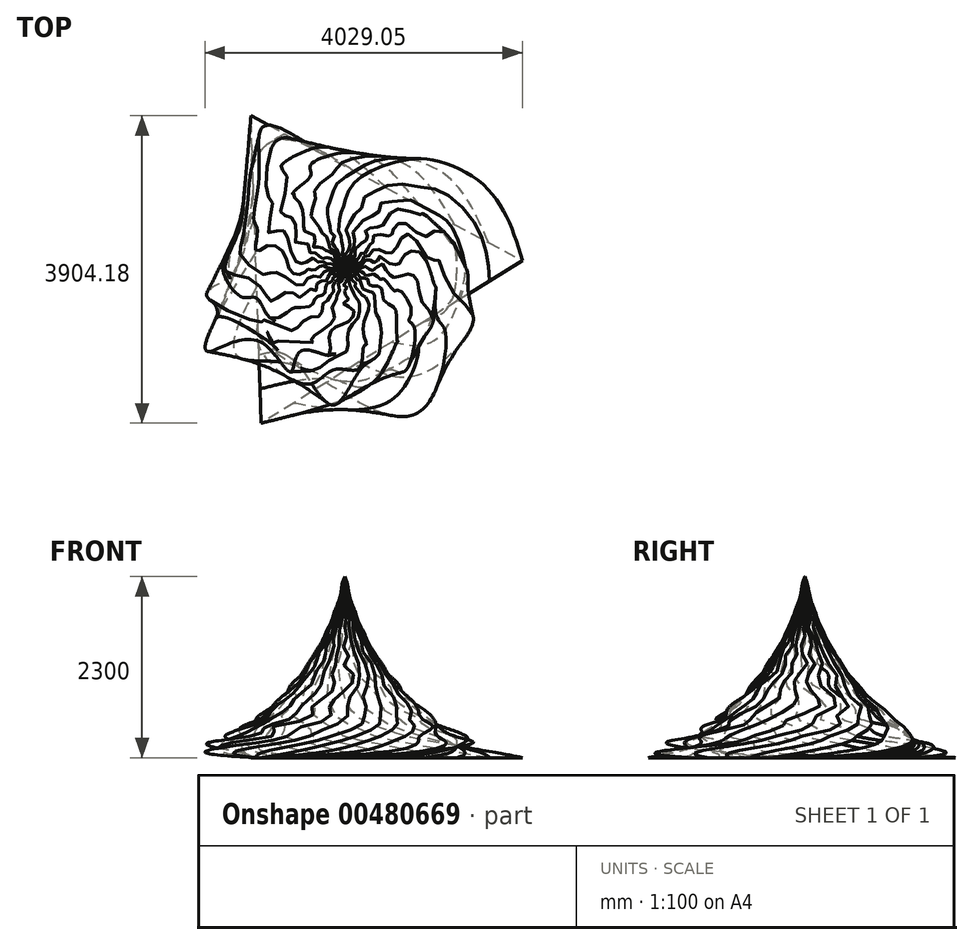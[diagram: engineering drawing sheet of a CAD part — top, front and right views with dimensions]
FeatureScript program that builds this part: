
annotation { "Feature Type Name" : "Feature", "Feature Type Description" : "" }
export const myFeature = defineFeature(function(context is Context, id is Id, definition is map)
    precondition{}
    {
        {
            var Q0;
            Q0=qCreatedBy(makeId("Top.planeOp"),FACE);
            var sketch = newSketch(context, id + "F0", { "sketchPlane" : qUnion([Q0])});
            skCircle(sketch, "E0.cCircle", {"center": v(0, 0) * mm, "radius": 2255.36 * mm, "construction": true});
            skLineSegment(sketch, "E0.0", {"start": v(2254.08, 76) * mm, "end": v(-1061.23, -1990.09) * mm});
            skLineSegment(sketch, "E0.1", {"start": v(-1061.23, -1990.09) * mm, "end": v(-1192.85, 1914.1) * mm});
            skLineSegment(sketch, "E0.2", {"start": v(-1192.85, 1914.1) * mm, "end": v(2254.08, 76) * mm});
            skSolve(sketch);
        }
        {
            var Q0;
            Q0=makeQuery(id+"F0.imprint","IMPRINT",FACE,{"disambiguationData":[TD([[makeQuery(id+"F0.imprint","IMPRINT",EDGE,{"derivedFrom":sQuery(id+"F0.wireOp",EDGE,"E0.0")}),-1.0]])]});
            cPlane(context, id + "F1", {"entities" : qUnion([Q0]), "cplaneType" : CPlaneType.OFFSET, "offset" : 100 * mm, "width" : 152.4 * mm, "height" : 152.4 * mm});
        }
        {
            var Q0;
            Q0=qCreatedBy(id+"F1.planeOp",FACE);
            var sketch = newSketch(context, id + "F2", { "sketchPlane" : qUnion([Q0])});
            skCircle(sketch, "E1.cCircle", {"center": v(0, 0) * mm, "radius": 2022.94 * mm, "construction": true});
            skLineSegment(sketch, "E1.0", {"start": v(-1078.65, 1711.37) * mm, "end": v(1711.37, 1078.65) * mm});
            skLineSegment(sketch, "E1.1", {"start": v(1711.37, 1078.65) * mm, "end": v(1078.65, -1711.37) * mm});
            skLineSegment(sketch, "E1.2", {"start": v(1078.65, -1711.37) * mm, "end": v(-1711.37, -1078.65) * mm});
            skLineSegment(sketch, "E1.3", {"start": v(-1711.37, -1078.65) * mm, "end": v(-1078.65, 1711.37) * mm});
            skSolve(sketch);
        }
        {
            var Q0;
            Q0=qCreatedBy(id+"F1.planeOp",FACE);
            cPlane(context, id + "F3", {"entities" : qUnion([Q0]), "cplaneType" : CPlaneType.OFFSET, "offset" : 100 * mm, "width" : 150 * mm, "height" : 150 * mm});
        }
        {
            var Q0;
            Q0=qCreatedBy(id+"F3.planeOp",FACE);
            var sketch = newSketch(context, id + "F4", { "sketchPlane" : qUnion([Q0])});
            skCircle(sketch, "E2.cCircle", {"center": v(0, 0) * mm, "radius": 1754.18 * mm, "construction": true});
            skLineSegment(sketch, "E2.0", {"start": v(-941.86, 1479.87) * mm, "end": v(1116.4, 1353.07) * mm});
            skLineSegment(sketch, "E2.1", {"start": v(1116.4, 1353.07) * mm, "end": v(1631.83, -643.63) * mm});
            skLineSegment(sketch, "E2.2", {"start": v(1631.83, -643.63) * mm, "end": v(-107.87, -1750.86) * mm});
            skLineSegment(sketch, "E2.3", {"start": v(-107.87, -1750.86) * mm, "end": v(-1698.5, -438.46) * mm});
            skLineSegment(sketch, "E2.4", {"start": v(-1698.5, -438.46) * mm, "end": v(-941.86, 1479.87) * mm});
            skSolve(sketch);
        }
        {
            var Q0;
            Q0=qCreatedBy(id+"F3.planeOp",FACE);
            cPlane(context, id + "F5", {"entities" : qUnion([Q0]), "cplaneType" : CPlaneType.OFFSET, "offset" : 100 * mm, "width" : 150 * mm, "height" : 150 * mm});
        }
        {
            var Q0;
            Q0=qCreatedBy(id+"F5.planeOp",FACE);
            var sketch = newSketch(context, id + "F6", { "sketchPlane" : qUnion([Q0])});
            skCircle(sketch, "E3.cCircle", {"center": v(0, 0) * mm, "radius": 1495.6 * mm, "construction": true});
            skLineSegment(sketch, "E3.0", {"start": v(-815.6, 1253.64) * mm, "end": v(677.89, 1333.14) * mm});
            skLineSegment(sketch, "E3.1", {"start": v(677.89, 1333.14) * mm, "end": v(1493.48, 79.5) * mm});
            skLineSegment(sketch, "E3.2", {"start": v(1493.48, 79.5) * mm, "end": v(815.6, -1253.64) * mm});
            skLineSegment(sketch, "E3.3", {"start": v(815.6, -1253.64) * mm, "end": v(-677.89, -1333.14) * mm});
            skLineSegment(sketch, "E3.4", {"start": v(-677.89, -1333.14) * mm, "end": v(-1493.48, -79.5) * mm});
            skLineSegment(sketch, "E3.5", {"start": v(-1493.48, -79.5) * mm, "end": v(-815.6, 1253.64) * mm});
            skSolve(sketch);
        }
        {
            var Q0;
            Q0=qCreatedBy(id+"F5.planeOp",FACE);
            cPlane(context, id + "F7", {"entities" : qUnion([Q0]), "cplaneType" : CPlaneType.OFFSET, "offset" : 100 * mm, "width" : 150 * mm, "height" : 150 * mm});
        }
        {
            var Q0;
            Q0=qCreatedBy(id+"F7.planeOp",FACE);
            var sketch = newSketch(context, id + "F8", { "sketchPlane" : qUnion([Q0])});
            skCircle(sketch, "E4.cCircle", {"center": v(0, 0) * mm, "radius": 1305.8 * mm, "construction": true});
            skLineSegment(sketch, "E4.0", {"start": v(-726.15, 1085.28) * mm, "end": v(395.76, 1244.39) * mm});
            skLineSegment(sketch, "E4.1", {"start": v(395.76, 1244.39) * mm, "end": v(1219.65, 466.45) * mm});
            skLineSegment(sketch, "E4.2", {"start": v(1219.65, 466.45) * mm, "end": v(1125.12, -662.74) * mm});
            skLineSegment(sketch, "E4.3", {"start": v(1125.12, -662.74) * mm, "end": v(183.35, -1292.87) * mm});
            skLineSegment(sketch, "E4.4", {"start": v(183.35, -1292.87) * mm, "end": v(-896.49, -949.44) * mm});
            skLineSegment(sketch, "E4.5", {"start": v(-896.49, -949.44) * mm, "end": v(-1301.25, 108.93) * mm});
            skLineSegment(sketch, "E4.6", {"start": v(-1301.25, 108.93) * mm, "end": v(-726.15, 1085.28) * mm});
            skSolve(sketch);
        }
        {
            var Q0;
            Q0=qCreatedBy(id+"F7.planeOp",FACE);
            cPlane(context, id + "F9", {"entities" : qUnion([Q0]), "cplaneType" : CPlaneType.OFFSET, "offset" : 100 * mm, "width" : 150 * mm, "height" : 150 * mm});
        }
        {
            var Q0;
            Q0=qCreatedBy(id+"F9.planeOp",FACE);
            var sketch = newSketch(context, id + "F10", { "sketchPlane" : qUnion([Q0])});
            skCircle(sketch, "E5.cCircle", {"center": v(0, 0) * mm, "radius": 1139.43 * mm, "construction": true});
            skLineSegment(sketch, "E5.0", {"start": v(-661.29, 927.9) * mm, "end": v(188.52, 1123.72) * mm});
            skLineSegment(sketch, "E5.1", {"start": v(188.52, 1123.72) * mm, "end": v(927.9, 661.29) * mm});
            skLineSegment(sketch, "E5.2", {"start": v(927.9, 661.29) * mm, "end": v(1123.72, -188.52) * mm});
            skLineSegment(sketch, "E5.3", {"start": v(1123.72, -188.52) * mm, "end": v(661.29, -927.9) * mm});
            skLineSegment(sketch, "E5.4", {"start": v(661.29, -927.9) * mm, "end": v(-188.52, -1123.72) * mm});
            skLineSegment(sketch, "E5.5", {"start": v(-188.52, -1123.72) * mm, "end": v(-927.9, -661.29) * mm});
            skLineSegment(sketch, "E5.6", {"start": v(-927.9, -661.29) * mm, "end": v(-1123.72, 188.52) * mm});
            skLineSegment(sketch, "E5.7", {"start": v(-1123.72, 188.52) * mm, "end": v(-661.29, 927.9) * mm});
            skSolve(sketch);
        }
        {
            var Q0;
            Q0=qCreatedBy(id+"F9.planeOp",FACE);
            cPlane(context, id + "F11", {"entities" : qUnion([Q0]), "cplaneType" : CPlaneType.OFFSET, "offset" : 100 * mm, "width" : 150 * mm, "height" : 150 * mm});
        }
        {
            var Q0;
            Q0=qCreatedBy(id+"F11.planeOp",FACE);
            var sketch = newSketch(context, id + "F12", { "sketchPlane" : qUnion([Q0])});
            skCircle(sketch, "E6.cCircle", {"center": v(0, 0) * mm, "radius": 1027.53 * mm, "construction": true});
            skLineSegment(sketch, "E6.0", {"start": v(-594.62, 838) * mm, "end": v(83.15, 1024.16) * mm});
            skLineSegment(sketch, "E6.1", {"start": v(83.15, 1024.16) * mm, "end": v(722.02, 731.1) * mm});
            skLineSegment(sketch, "E6.2", {"start": v(722.02, 731.1) * mm, "end": v(1023.04, 95.95) * mm});
            skLineSegment(sketch, "E6.3", {"start": v(1023.04, 95.95) * mm, "end": v(845.37, -584.1) * mm});
            skLineSegment(sketch, "E6.4", {"start": v(845.37, -584.1) * mm, "end": v(272.15, -990.84) * mm});
            skLineSegment(sketch, "E6.5", {"start": v(272.15, -990.84) * mm, "end": v(-428.42, -933.96) * mm});
            skLineSegment(sketch, "E6.6", {"start": v(-428.42, -933.96) * mm, "end": v(-928.53, -440.07) * mm});
            skLineSegment(sketch, "E6.7", {"start": v(-928.53, -440.07) * mm, "end": v(-994.16, 259.73) * mm});
            skLineSegment(sketch, "E6.8", {"start": v(-994.16, 259.73) * mm, "end": v(-594.62, 838) * mm});
            skSolve(sketch);
        }
        {
            var Q0;
            Q0=qCreatedBy(id+"F11.planeOp",FACE);
            cPlane(context, id + "F13", {"entities" : qUnion([Q0]), "cplaneType" : CPlaneType.OFFSET, "offset" : 100 * mm, "width" : 150 * mm, "height" : 150 * mm});
        }
        {
            var Q0;
            Q0=qCreatedBy(id+"F13.planeOp",FACE);
            cPlane(context, id + "F14", {"entities" : qUnion([Q0]), "cplaneType" : CPlaneType.OFFSET, "offset" : 100 * mm, "width" : 150 * mm, "height" : 150 * mm});
        }
        {
            var Q0;
            Q0=qCreatedBy(id+"F14.planeOp",FACE);
            var sketch = newSketch(context, id + "F15", { "sketchPlane" : qUnion([Q0])});
            skCircle(sketch, "E7.cCircle", {"center": v(0, 0) * mm, "radius": 779.03 * mm, "construction": true});
            skLineSegment(sketch, "E7.0", {"start": v(-431.52, 648.6) * mm, "end": v(-12.36, 778.93) * mm});
            skLineSegment(sketch, "E7.1", {"start": v(-12.36, 778.93) * mm, "end": v(410.72, 661.96) * mm});
            skLineSegment(sketch, "E7.2", {"start": v(410.72, 661.96) * mm, "end": v(703.4, 334.82) * mm});
            skLineSegment(sketch, "E7.3", {"start": v(703.4, 334.82) * mm, "end": v(772.76, -98.62) * mm});
            skLineSegment(sketch, "E7.4", {"start": v(772.76, -98.62) * mm, "end": v(596.77, -500.75) * mm});
            skLineSegment(sketch, "E7.5", {"start": v(596.77, -500.75) * mm, "end": v(231.3, -743.9) * mm});
            skLineSegment(sketch, "E7.6", {"start": v(231.3, -743.9) * mm, "end": v(-207.6, -750.86) * mm});
            skLineSegment(sketch, "E7.7", {"start": v(-207.6, -750.86) * mm, "end": v(-580.58, -519.43) * mm});
            skLineSegment(sketch, "E7.8", {"start": v(-580.58, -519.43) * mm, "end": v(-769.24, -123.09) * mm});
            skLineSegment(sketch, "E7.9", {"start": v(-769.24, -123.09) * mm, "end": v(-713.68, 312.34) * mm});
            skLineSegment(sketch, "E7.10", {"start": v(-713.68, 312.34) * mm, "end": v(-431.52, 648.6) * mm});
            skSolve(sketch);
        }
        {
            var Q0;
            Q0=qCreatedBy(id+"F14.planeOp",FACE);
            cPlane(context, id + "F16", {"entities" : qUnion([Q0]), "cplaneType" : CPlaneType.OFFSET, "offset" : 100 * mm, "width" : 150 * mm, "height" : 150 * mm});
        }
        {
            var Q0;
            Q0=qCreatedBy(id+"F16.planeOp",FACE);
            var sketch = newSketch(context, id + "F17", { "sketchPlane" : qUnion([Q0])});
            skCircle(sketch, "E8.cCircle", {"center": v(0, 0) * mm, "radius": 703.15 * mm, "construction": true});
            skLineSegment(sketch, "E8.0", {"start": v(-389.43, 585.46) * mm, "end": v(-44.53, 701.74) * mm});
            skLineSegment(sketch, "E8.1", {"start": v(-44.53, 701.74) * mm, "end": v(312.3, 629.99) * mm});
            skLineSegment(sketch, "E8.2", {"start": v(312.3, 629.99) * mm, "end": v(585.46, 389.43) * mm});
            skLineSegment(sketch, "E8.3", {"start": v(585.46, 389.43) * mm, "end": v(701.74, 44.53) * mm});
            skLineSegment(sketch, "E8.4", {"start": v(701.74, 44.53) * mm, "end": v(629.99, -312.3) * mm});
            skLineSegment(sketch, "E8.5", {"start": v(629.99, -312.3) * mm, "end": v(389.43, -585.46) * mm});
            skLineSegment(sketch, "E8.6", {"start": v(389.43, -585.46) * mm, "end": v(44.53, -701.74) * mm});
            skLineSegment(sketch, "E8.7", {"start": v(44.53, -701.74) * mm, "end": v(-312.3, -629.99) * mm});
            skLineSegment(sketch, "E8.8", {"start": v(-312.3, -629.99) * mm, "end": v(-585.46, -389.43) * mm});
            skLineSegment(sketch, "E8.9", {"start": v(-585.46, -389.43) * mm, "end": v(-701.74, -44.53) * mm});
            skLineSegment(sketch, "E8.10", {"start": v(-701.74, -44.53) * mm, "end": v(-629.99, 312.3) * mm});
            skLineSegment(sketch, "E8.11", {"start": v(-629.99, 312.3) * mm, "end": v(-389.43, 585.46) * mm});
            skSolve(sketch);
        }
        {
            var Q0;
            Q0=qCreatedBy(id+"F16.planeOp",FACE);
            cPlane(context, id + "F18", {"entities" : qUnion([Q0]), "cplaneType" : CPlaneType.OFFSET, "offset" : 100 * mm, "width" : 150 * mm, "height" : 150 * mm});
        }
        {
            var Q0;
            Q0=qCreatedBy(id+"F18.planeOp",FACE);
            cPlane(context, id + "F19", {"entities" : qUnion([Q0]), "cplaneType" : CPlaneType.OFFSET, "offset" : 100 * mm, "width" : 150 * mm, "height" : 150 * mm});
        }
        {
            var Q0;
            Q0=qCreatedBy(id+"F19.planeOp",FACE);
            var sketch = newSketch(context, id + "F20", { "sketchPlane" : qUnion([Q0])});
            skCircle(sketch, "E9.cCircle", {"center": v(0, 0) * mm, "radius": 528.05 * mm, "construction": true});
            skLineSegment(sketch, "E9.0", {"start": v(-294.73, 438.15) * mm, "end": v(-75.44, 522.63) * mm});
            skLineSegment(sketch, "E9.1", {"start": v(-75.44, 522.63) * mm, "end": v(158.8, 503.6) * mm});
            skLineSegment(sketch, "E9.2", {"start": v(158.8, 503.6) * mm, "end": v(361.58, 384.83) * mm});
            skLineSegment(sketch, "E9.3", {"start": v(361.58, 384.83) * mm, "end": v(492.74, 189.84) * mm});
            skLineSegment(sketch, "E9.4", {"start": v(492.74, 189.84) * mm, "end": v(526.32, -42.75) * mm});
            skLineSegment(sketch, "E9.5", {"start": v(526.32, -42.75) * mm, "end": v(455.65, -266.88) * mm});
            skLineSegment(sketch, "E9.6", {"start": v(455.65, -266.88) * mm, "end": v(294.73, -438.15) * mm});
            skLineSegment(sketch, "E9.7", {"start": v(294.73, -438.15) * mm, "end": v(75.44, -522.63) * mm});
            skLineSegment(sketch, "E9.8", {"start": v(75.44, -522.63) * mm, "end": v(-158.8, -503.6) * mm});
            skLineSegment(sketch, "E9.9", {"start": v(-158.8, -503.6) * mm, "end": v(-361.58, -384.83) * mm});
            skLineSegment(sketch, "E9.10", {"start": v(-361.58, -384.83) * mm, "end": v(-492.74, -189.84) * mm});
            skLineSegment(sketch, "E9.11", {"start": v(-492.74, -189.84) * mm, "end": v(-526.32, 42.75) * mm});
            skLineSegment(sketch, "E9.12", {"start": v(-526.32, 42.75) * mm, "end": v(-455.65, 266.88) * mm});
            skLineSegment(sketch, "E9.13", {"start": v(-455.65, 266.88) * mm, "end": v(-294.73, 438.15) * mm});
            skSolve(sketch);
        }
        {
            var Q0;
            Q0=qCreatedBy(id+"F19.planeOp",FACE);
            cPlane(context, id + "F21", {"entities" : qUnion([Q0]), "cplaneType" : CPlaneType.OFFSET, "offset" : 100 * mm, "width" : 150 * mm, "height" : 150 * mm});
        }
        {
            var Q0;
            Q0=qCreatedBy(id+"F21.planeOp",FACE);
            var sketch = newSketch(context, id + "F22", { "sketchPlane" : qUnion([Q0])});
            skCircle(sketch, "E10.cCircle", {"center": v(0, 0) * mm, "radius": 471.14 * mm, "construction": true});
            skLineSegment(sketch, "E10.0", {"start": v(-263.16, 390.8) * mm, "end": v(-81.46, 464.05) * mm});
            skLineSegment(sketch, "E10.1", {"start": v(-81.46, 464.05) * mm, "end": v(114.33, 457.06) * mm});
            skLineSegment(sketch, "E10.2", {"start": v(114.33, 457.06) * mm, "end": v(290.35, 371.04) * mm});
            skLineSegment(sketch, "E10.3", {"start": v(290.35, 371.04) * mm, "end": v(416.16, 220.87) * mm});
            skLineSegment(sketch, "E10.4", {"start": v(416.16, 220.87) * mm, "end": v(470.02, 32.5) * mm});
            skLineSegment(sketch, "E10.5", {"start": v(470.02, 32.5) * mm, "end": v(442.6, -161.48) * mm});
            skLineSegment(sketch, "E10.6", {"start": v(442.6, -161.48) * mm, "end": v(338.66, -327.54) * mm});
            skLineSegment(sketch, "E10.7", {"start": v(338.66, -327.54) * mm, "end": v(176.16, -436.97) * mm});
            skLineSegment(sketch, "E10.8", {"start": v(176.16, -436.97) * mm, "end": v(-16.8, -470.84) * mm});
            skLineSegment(sketch, "E10.9", {"start": v(-16.8, -470.84) * mm, "end": v(-206.86, -423.3) * mm});
            skLineSegment(sketch, "E10.10", {"start": v(-206.86, -423.3) * mm, "end": v(-361.15, -302.57) * mm});
            skLineSegment(sketch, "E10.11", {"start": v(-361.15, -302.57) * mm, "end": v(-452.99, -129.52) * mm});
            skLineSegment(sketch, "E10.12", {"start": v(-452.99, -129.52) * mm, "end": v(-466.5, 65.93) * mm});
            skLineSegment(sketch, "E10.13", {"start": v(-466.5, 65.93) * mm, "end": v(-399.36, 249.97) * mm});
            skLineSegment(sketch, "E10.14", {"start": v(-399.36, 249.97) * mm, "end": v(-263.16, 390.8) * mm});
            skSolve(sketch);
        }
        {
            var Q0;
            Q0=qCreatedBy(id+"F21.planeOp",FACE);
            cPlane(context, id + "F23", {"entities" : qUnion([Q0]), "cplaneType" : CPlaneType.OFFSET, "offset" : 100 * mm, "width" : 150 * mm, "height" : 150 * mm});
        }
        {
            var Q0;
            Q0=qCreatedBy(id+"F23.planeOp",FACE);
            var sketch = newSketch(context, id + "F24", { "sketchPlane" : qUnion([Q0])});
            skCircle(sketch, "E11.cCircle", {"center": v(0, 0) * mm, "radius": 402 * mm, "construction": true});
            skLineSegment(sketch, "E11.0", {"start": v(-200.02, 348.7) * mm, "end": v(-51.36, 398.7) * mm});
            skLineSegment(sketch, "E11.1", {"start": v(-51.36, 398.7) * mm, "end": v(105.13, 388.01) * mm});
            skLineSegment(sketch, "E11.2", {"start": v(105.13, 388.01) * mm, "end": v(245.62, 318.24) * mm});
            skLineSegment(sketch, "E11.3", {"start": v(245.62, 318.24) * mm, "end": v(348.7, 200.02) * mm});
            skLineSegment(sketch, "E11.4", {"start": v(348.7, 200.02) * mm, "end": v(398.7, 51.36) * mm});
            skLineSegment(sketch, "E11.5", {"start": v(398.7, 51.36) * mm, "end": v(388.01, -105.13) * mm});
            skLineSegment(sketch, "E11.6", {"start": v(388.01, -105.13) * mm, "end": v(318.24, -245.62) * mm});
            skLineSegment(sketch, "E11.7", {"start": v(318.24, -245.62) * mm, "end": v(200.02, -348.7) * mm});
            skLineSegment(sketch, "E11.8", {"start": v(200.02, -348.7) * mm, "end": v(51.36, -398.7) * mm});
            skLineSegment(sketch, "E11.9", {"start": v(51.36, -398.7) * mm, "end": v(-105.13, -388.01) * mm});
            skLineSegment(sketch, "E11.10", {"start": v(-105.13, -388.01) * mm, "end": v(-245.62, -318.24) * mm});
            skLineSegment(sketch, "E11.11", {"start": v(-245.62, -318.24) * mm, "end": v(-348.7, -200.02) * mm});
            skLineSegment(sketch, "E11.12", {"start": v(-348.7, -200.02) * mm, "end": v(-398.7, -51.36) * mm});
            skLineSegment(sketch, "E11.13", {"start": v(-398.7, -51.36) * mm, "end": v(-388.01, 105.13) * mm});
            skLineSegment(sketch, "E11.14", {"start": v(-388.01, 105.13) * mm, "end": v(-318.24, 245.62) * mm});
            skLineSegment(sketch, "E11.15", {"start": v(-318.24, 245.62) * mm, "end": v(-200.02, 348.7) * mm});
            skSolve(sketch);
        }
        {
            var Q0;
            Q0=qCreatedBy(id+"F23.planeOp",FACE);
            cPlane(context, id + "F25", {"entities" : qUnion([Q0]), "cplaneType" : CPlaneType.OFFSET, "offset" : 100 * mm, "width" : 150 * mm, "height" : 150 * mm});
        }
        {
            var Q0;
            Q0=qCreatedBy(id+"F25.planeOp",FACE);
            var sketch = newSketch(context, id + "F26", { "sketchPlane" : qUnion([Q0])});
            skCircle(sketch, "E12.cCircle", {"center": v(0, 0) * mm, "radius": 338.09 * mm, "construction": true});
            skLineSegment(sketch, "E12.0", {"start": v(-163.2, 296.1) * mm, "end": v(-45.21, 335.05) * mm});
            skLineSegment(sketch, "E12.1", {"start": v(-45.21, 335.05) * mm, "end": v(78.87, 328.76) * mm});
            skLineSegment(sketch, "E12.2", {"start": v(78.87, 328.76) * mm, "end": v(192.3, 278.07) * mm});
            skLineSegment(sketch, "E12.3", {"start": v(192.3, 278.07) * mm, "end": v(279.77, 189.82) * mm});
            skLineSegment(sketch, "E12.4", {"start": v(279.77, 189.82) * mm, "end": v(329.45, 75.94) * mm});
            skLineSegment(sketch, "E12.5", {"start": v(329.45, 75.94) * mm, "end": v(334.64, -48.2) * mm});
            skLineSegment(sketch, "E12.6", {"start": v(334.64, -48.2) * mm, "end": v(294.63, -165.83) * mm});
            skLineSegment(sketch, "E12.7", {"start": v(294.63, -165.83) * mm, "end": v(214.82, -261.06) * mm});
            skLineSegment(sketch, "E12.8", {"start": v(214.82, -261.06) * mm, "end": v(106.01, -321.04) * mm});
            skLineSegment(sketch, "E12.9", {"start": v(106.01, -321.04) * mm, "end": v(-17.12, -337.66) * mm});
            skLineSegment(sketch, "E12.10", {"start": v(-17.12, -337.66) * mm, "end": v(-137.94, -308.67) * mm});
            skLineSegment(sketch, "E12.11", {"start": v(-137.94, -308.67) * mm, "end": v(-240.13, -238) * mm});
            skLineSegment(sketch, "E12.12", {"start": v(-240.13, -238) * mm, "end": v(-309.89, -135.18) * mm});
            skLineSegment(sketch, "E12.13", {"start": v(-309.89, -135.18) * mm, "end": v(-337.8, -14.1) * mm});
            skLineSegment(sketch, "E12.14", {"start": v(-337.8, -14.1) * mm, "end": v(-320.08, 108.87) * mm});
            skLineSegment(sketch, "E12.15", {"start": v(-320.08, 108.87) * mm, "end": v(-259.14, 217.15) * mm});
            skLineSegment(sketch, "E12.16", {"start": v(-259.14, 217.15) * mm, "end": v(-163.2, 296.1) * mm});
            skSolve(sketch);
        }
        {
            var Q0;
            Q0=qCreatedBy(id+"F25.planeOp",FACE);
            cPlane(context, id + "F27", {"entities" : qUnion([Q0]), "cplaneType" : CPlaneType.OFFSET, "offset" : 100 * mm, "width" : 150 * mm, "height" : 150 * mm});
        }
        {
            var Q0;
            Q0=qCreatedBy(id+"F27.planeOp",FACE);
            var sketch = newSketch(context, id + "F28", { "sketchPlane" : qUnion([Q0])});
            skCircle(sketch, "E13.cCircle", {"center": v(0, 0) * mm, "radius": 279 * mm, "construction": true});
            skLineSegment(sketch, "E13.0", {"start": v(-126.37, 248.74) * mm, "end": v(-33.67, 276.96) * mm});
            skLineSegment(sketch, "E13.1", {"start": v(-33.67, 276.96) * mm, "end": v(63.09, 271.77) * mm});
            skLineSegment(sketch, "E13.2", {"start": v(63.09, 271.77) * mm, "end": v(152.23, 233.8) * mm});
            skLineSegment(sketch, "E13.3", {"start": v(152.23, 233.8) * mm, "end": v(223.02, 167.64) * mm});
            skLineSegment(sketch, "E13.4", {"start": v(223.02, 167.64) * mm, "end": v(266.9, 81.25) * mm});
            skLineSegment(sketch, "E13.5", {"start": v(266.9, 81.25) * mm, "end": v(278.6, -14.93) * mm});
            skLineSegment(sketch, "E13.6", {"start": v(278.6, -14.93) * mm, "end": v(256.7, -109.32) * mm});
            skLineSegment(sketch, "E13.7", {"start": v(256.7, -109.32) * mm, "end": v(203.82, -190.52) * mm});
            skLineSegment(sketch, "E13.8", {"start": v(203.82, -190.52) * mm, "end": v(126.37, -248.74) * mm});
            skLineSegment(sketch, "E13.9", {"start": v(126.37, -248.74) * mm, "end": v(33.67, -276.96) * mm});
            skLineSegment(sketch, "E13.10", {"start": v(33.67, -276.96) * mm, "end": v(-63.09, -271.77) * mm});
            skLineSegment(sketch, "E13.11", {"start": v(-63.09, -271.77) * mm, "end": v(-152.23, -233.8) * mm});
            skLineSegment(sketch, "E13.12", {"start": v(-152.23, -233.8) * mm, "end": v(-223.02, -167.64) * mm});
            skLineSegment(sketch, "E13.13", {"start": v(-223.02, -167.64) * mm, "end": v(-266.9, -81.25) * mm});
            skLineSegment(sketch, "E13.14", {"start": v(-266.9, -81.25) * mm, "end": v(-278.6, 14.93) * mm});
            skLineSegment(sketch, "E13.15", {"start": v(-278.6, 14.93) * mm, "end": v(-256.7, 109.32) * mm});
            skLineSegment(sketch, "E13.16", {"start": v(-256.7, 109.32) * mm, "end": v(-203.82, 190.52) * mm});
            skLineSegment(sketch, "E13.17", {"start": v(-203.82, 190.52) * mm, "end": v(-126.37, 248.74) * mm});
            skSolve(sketch);
        }
        {
            var Q0;
            Q0=qCreatedBy(id+"F27.planeOp",FACE);
            cPlane(context, id + "F29", {"entities" : qUnion([Q0]), "cplaneType" : CPlaneType.OFFSET, "offset" : 100 * mm, "width" : 150 * mm, "height" : 150 * mm});
        }
        {
            var Q0;
            Q0=qCreatedBy(id+"F29.planeOp",FACE);
            var sketch = newSketch(context, id + "F30", { "sketchPlane" : qUnion([Q0])});
            skCircle(sketch, "E14.cCircle", {"center": v(0, 0) * mm, "radius": 239.12 * mm, "construction": true});
            skLineSegment(sketch, "E14.0", {"start": v(-100.06, 217.17) * mm, "end": v(-24.12, 237.9) * mm});
            skLineSegment(sketch, "E14.1", {"start": v(-24.12, 237.9) * mm, "end": v(54.43, 232.84) * mm});
            skLineSegment(sketch, "E14.2", {"start": v(54.43, 232.84) * mm, "end": v(127.08, 202.55) * mm});
            skLineSegment(sketch, "E14.3", {"start": v(127.08, 202.55) * mm, "end": v(185.97, 150.31) * mm});
            skLineSegment(sketch, "E14.4", {"start": v(185.97, 150.31) * mm, "end": v(224.7, 81.79) * mm});
            skLineSegment(sketch, "E14.5", {"start": v(224.7, 81.79) * mm, "end": v(239.08, 4.4) * mm});
            skLineSegment(sketch, "E14.6", {"start": v(239.08, 4.4) * mm, "end": v(227.55, -73.47) * mm});
            skLineSegment(sketch, "E14.7", {"start": v(227.55, -73.47) * mm, "end": v(191.36, -143.38) * mm});
            skLineSegment(sketch, "E14.8", {"start": v(191.36, -143.38) * mm, "end": v(134.44, -197.74) * mm});
            skLineSegment(sketch, "E14.9", {"start": v(134.44, -197.74) * mm, "end": v(62.95, -230.68) * mm});
            skLineSegment(sketch, "E14.10", {"start": v(62.95, -230.68) * mm, "end": v(-15.36, -238.62) * mm});
            skLineSegment(sketch, "E14.11", {"start": v(-15.36, -238.62) * mm, "end": v(-92.01, -220.7) * mm});
            skLineSegment(sketch, "E14.12", {"start": v(-92.01, -220.7) * mm, "end": v(-158.69, -178.87) * mm});
            skLineSegment(sketch, "E14.13", {"start": v(-158.69, -178.87) * mm, "end": v(-208.17, -117.65) * mm});
            skLineSegment(sketch, "E14.14", {"start": v(-208.17, -117.65) * mm, "end": v(-235.1, -43.69) * mm});
            skLineSegment(sketch, "E14.15", {"start": v(-235.1, -43.69) * mm, "end": v(-236.54, 35.02) * mm});
            skLineSegment(sketch, "E14.16", {"start": v(-236.54, 35.02) * mm, "end": v(-212.35, 109.92) * mm});
            skLineSegment(sketch, "E14.17", {"start": v(-212.35, 109.92) * mm, "end": v(-165.16, 172.92) * mm});
            skLineSegment(sketch, "E14.18", {"start": v(-165.16, 172.92) * mm, "end": v(-100.06, 217.17) * mm});
            skSolve(sketch);
        }
        {
            var Q0;
            Q0=qCreatedBy(id+"F29.planeOp",FACE);
            cPlane(context, id + "F31", {"entities" : qUnion([Q0]), "cplaneType" : CPlaneType.OFFSET, "offset" : 100 * mm, "width" : 150 * mm, "height" : 150 * mm});
        }
        {
            var Q0;
            Q0=qCreatedBy(id+"F31.planeOp",FACE);
            var sketch = newSketch(context, id + "F32", { "sketchPlane" : qUnion([Q0])});
            skCircle(sketch, "E15.cCircle", {"center": v(0, 0) * mm, "radius": 187.3 * mm, "construction": true});
            skLineSegment(sketch, "E15.0", {"start": v(-79.02, 169.82) * mm, "end": v(-22.67, 185.93) * mm});
            skLineSegment(sketch, "E15.1", {"start": v(-22.67, 185.93) * mm, "end": v(35.9, 183.83) * mm});
            skLineSegment(sketch, "E15.2", {"start": v(35.9, 183.83) * mm, "end": v(90.95, 163.74) * mm});
            skLineSegment(sketch, "E15.3", {"start": v(90.95, 163.74) * mm, "end": v(137.1, 127.63) * mm});
            skLineSegment(sketch, "E15.4", {"start": v(137.1, 127.63) * mm, "end": v(169.82, 79.02) * mm});
            skLineSegment(sketch, "E15.5", {"start": v(169.82, 79.02) * mm, "end": v(185.93, 22.67) * mm});
            skLineSegment(sketch, "E15.6", {"start": v(185.93, 22.67) * mm, "end": v(183.83, -35.9) * mm});
            skLineSegment(sketch, "E15.7", {"start": v(183.83, -35.9) * mm, "end": v(163.74, -90.95) * mm});
            skLineSegment(sketch, "E15.8", {"start": v(163.74, -90.95) * mm, "end": v(127.63, -137.1) * mm});
            skLineSegment(sketch, "E15.9", {"start": v(127.63, -137.1) * mm, "end": v(79.02, -169.82) * mm});
            skLineSegment(sketch, "E15.10", {"start": v(79.02, -169.82) * mm, "end": v(22.67, -185.93) * mm});
            skLineSegment(sketch, "E15.11", {"start": v(22.67, -185.93) * mm, "end": v(-35.9, -183.83) * mm});
            skLineSegment(sketch, "E15.12", {"start": v(-35.9, -183.83) * mm, "end": v(-90.95, -163.74) * mm});
            skLineSegment(sketch, "E15.13", {"start": v(-90.95, -163.74) * mm, "end": v(-137.1, -127.63) * mm});
            skLineSegment(sketch, "E15.14", {"start": v(-137.1, -127.63) * mm, "end": v(-169.82, -79.02) * mm});
            skLineSegment(sketch, "E15.15", {"start": v(-169.82, -79.02) * mm, "end": v(-185.93, -22.67) * mm});
            skLineSegment(sketch, "E15.16", {"start": v(-185.93, -22.67) * mm, "end": v(-183.83, 35.9) * mm});
            skLineSegment(sketch, "E15.17", {"start": v(-183.83, 35.9) * mm, "end": v(-163.74, 90.95) * mm});
            skLineSegment(sketch, "E15.18", {"start": v(-163.74, 90.95) * mm, "end": v(-127.63, 137.1) * mm});
            skLineSegment(sketch, "E15.19", {"start": v(-127.63, 137.1) * mm, "end": v(-79.02, 169.82) * mm});
            skSolve(sketch);
        }
        {
            var Q0;
            Q0=qCreatedBy(id+"F31.planeOp",FACE);
            cPlane(context, id + "F33", {"entities" : qUnion([Q0]), "cplaneType" : CPlaneType.OFFSET, "offset" : 100 * mm, "width" : 150 * mm, "height" : 150 * mm});
        }
        {
            var Q0;
            Q0=qCreatedBy(id+"F33.planeOp",FACE);
            var sketch = newSketch(context, id + "F34", { "sketchPlane" : qUnion([Q0])});
            skCircle(sketch, "E16.cCircle", {"center": v(0, 0) * mm, "radius": 150.2 * mm, "construction": true});
            skLineSegment(sketch, "E16.0", {"start": v(-79.02, 127.73) * mm, "end": v(-37.86, 145.35) * mm});
            skLineSegment(sketch, "E16.1", {"start": v(-37.86, 145.35) * mm, "end": v(6.67, 150.05) * mm});
            skLineSegment(sketch, "E16.2", {"start": v(6.67, 150.05) * mm, "end": v(50.6, 141.42) * mm});
            skLineSegment(sketch, "E16.3", {"start": v(50.6, 141.42) * mm, "end": v(90.04, 120.22) * mm});
            skLineSegment(sketch, "E16.4", {"start": v(90.04, 120.22) * mm, "end": v(121.47, 88.34) * mm});
            skLineSegment(sketch, "E16.5", {"start": v(121.47, 88.34) * mm, "end": v(142.11, 48.61) * mm});
            skLineSegment(sketch, "E16.6", {"start": v(142.11, 48.61) * mm, "end": v(150.13, 4.56) * mm});
            skLineSegment(sketch, "E16.7", {"start": v(150.13, 4.56) * mm, "end": v(144.8, -39.9) * mm});
            skLineSegment(sketch, "E16.8", {"start": v(144.8, -39.9) * mm, "end": v(126.61, -80.8) * mm});
            skLineSegment(sketch, "E16.9", {"start": v(126.61, -80.8) * mm, "end": v(97.17, -114.53) * mm});
            skLineSegment(sketch, "E16.10", {"start": v(97.17, -114.53) * mm, "end": v(59.1, -138.08) * mm});
            skLineSegment(sketch, "E16.11", {"start": v(59.1, -138.08) * mm, "end": v(15.77, -149.37) * mm});
            skLineSegment(sketch, "E16.12", {"start": v(15.77, -149.37) * mm, "end": v(-28.96, -147.38) * mm});
            skLineSegment(sketch, "E16.13", {"start": v(-28.96, -147.38) * mm, "end": v(-71.11, -132.3) * mm});
            skLineSegment(sketch, "E16.14", {"start": v(-71.11, -132.3) * mm, "end": v(-106.95, -105.46) * mm});
            skLineSegment(sketch, "E16.15", {"start": v(-106.95, -105.46) * mm, "end": v(-133.28, -69.25) * mm});
            skLineSegment(sketch, "E16.16", {"start": v(-133.28, -69.25) * mm, "end": v(-147.77, -26.89) * mm});
            skLineSegment(sketch, "E16.17", {"start": v(-147.77, -26.89) * mm, "end": v(-149.13, 17.86) * mm});
            skLineSegment(sketch, "E16.18", {"start": v(-149.13, 17.86) * mm, "end": v(-137.24, 61.03) * mm});
            skLineSegment(sketch, "E16.19", {"start": v(-137.24, 61.03) * mm, "end": v(-113.16, 98.77) * mm});
            skLineSegment(sketch, "E16.20", {"start": v(-113.16, 98.77) * mm, "end": v(-79.02, 127.73) * mm});
            skSolve(sketch);
        }
        {
            var Q0;
            Q0=qCreatedBy(id+"F33.planeOp",FACE);
            cPlane(context, id + "F35", {"entities" : qUnion([Q0]), "cplaneType" : CPlaneType.OFFSET, "offset" : 100 * mm, "width" : 150 * mm, "height" : 150 * mm});
        }
        {
            var Q0;
            Q0=qCreatedBy(id+"F35.planeOp",FACE);
            var sketch = newSketch(context, id + "F36", { "sketchPlane" : qUnion([Q0])});
            skCircle(sketch, "E17.cCircle", {"center": v(0, 0) * mm, "radius": 113.82 * mm, "construction": true});
            skLineSegment(sketch, "E17.0", {"start": v(-68.5, 90.9) * mm, "end": v(-40.1, 106.52) * mm});
            skLineSegment(sketch, "E17.1", {"start": v(-40.1, 106.52) * mm, "end": v(-8.47, 113.5) * mm});
            skLineSegment(sketch, "E17.2", {"start": v(-8.47, 113.5) * mm, "end": v(23.85, 111.3) * mm});
            skLineSegment(sketch, "E17.3", {"start": v(23.85, 111.3) * mm, "end": v(54.24, 100.07) * mm});
            skLineSegment(sketch, "E17.4", {"start": v(54.24, 100.07) * mm, "end": v(80.23, 80.73) * mm});
            skLineSegment(sketch, "E17.5", {"start": v(80.23, 80.73) * mm, "end": v(99.73, 54.86) * mm});
            skLineSegment(sketch, "E17.6", {"start": v(99.73, 54.86) * mm, "end": v(111.14, 24.54) * mm});
            skLineSegment(sketch, "E17.7", {"start": v(111.14, 24.54) * mm, "end": v(113.55, -7.77) * mm});
            skLineSegment(sketch, "E17.8", {"start": v(113.55, -7.77) * mm, "end": v(106.77, -39.44) * mm});
            skLineSegment(sketch, "E17.9", {"start": v(106.77, -39.44) * mm, "end": v(91.33, -67.93) * mm});
            skLineSegment(sketch, "E17.10", {"start": v(91.33, -67.93) * mm, "end": v(68.5, -90.9) * mm});
            skLineSegment(sketch, "E17.11", {"start": v(68.5, -90.9) * mm, "end": v(40.1, -106.52) * mm});
            skLineSegment(sketch, "E17.12", {"start": v(40.1, -106.52) * mm, "end": v(8.47, -113.5) * mm});
            skLineSegment(sketch, "E17.13", {"start": v(8.47, -113.5) * mm, "end": v(-23.85, -111.3) * mm});
            skLineSegment(sketch, "E17.14", {"start": v(-23.85, -111.3) * mm, "end": v(-54.24, -100.07) * mm});
            skLineSegment(sketch, "E17.15", {"start": v(-54.24, -100.07) * mm, "end": v(-80.23, -80.73) * mm});
            skLineSegment(sketch, "E17.16", {"start": v(-80.23, -80.73) * mm, "end": v(-99.73, -54.86) * mm});
            skLineSegment(sketch, "E17.17", {"start": v(-99.73, -54.86) * mm, "end": v(-111.14, -24.54) * mm});
            skLineSegment(sketch, "E17.18", {"start": v(-111.14, -24.54) * mm, "end": v(-113.55, 7.77) * mm});
            skLineSegment(sketch, "E17.19", {"start": v(-113.55, 7.77) * mm, "end": v(-106.77, 39.44) * mm});
            skLineSegment(sketch, "E17.20", {"start": v(-106.77, 39.44) * mm, "end": v(-91.33, 67.93) * mm});
            skLineSegment(sketch, "E17.21", {"start": v(-91.33, 67.93) * mm, "end": v(-68.5, 90.9) * mm});
            skSolve(sketch);
        }
        {
            var Q0;
            Q0=qCreatedBy(id+"F35.planeOp",FACE);
            cPlane(context, id + "F37", {"entities" : qUnion([Q0]), "cplaneType" : CPlaneType.OFFSET, "offset" : 100 * mm, "width" : 150 * mm, "height" : 150 * mm});
        }
        {
            var Q0;
            Q0=qCreatedBy(id+"F37.planeOp",FACE);
            var sketch = newSketch(context, id + "F38", { "sketchPlane" : qUnion([Q0])});
            skCircle(sketch, "E18.cCircle", {"center": v(0, 0) * mm, "radius": 75.12 * mm, "construction": true});
            skLineSegment(sketch, "E18.0", {"start": v(0, 75.12) * mm, "end": v(20.27, 72.33) * mm});
            skLineSegment(sketch, "E18.1", {"start": v(20.27, 72.33) * mm, "end": v(39.03, 64.18) * mm});
            skLineSegment(sketch, "E18.2", {"start": v(39.03, 64.18) * mm, "end": v(54.9, 51.27) * mm});
            skLineSegment(sketch, "E18.3", {"start": v(54.9, 51.27) * mm, "end": v(66.7, 34.56) * mm});
            skLineSegment(sketch, "E18.4", {"start": v(66.7, 34.56) * mm, "end": v(73.55, 15.28) * mm});
            skLineSegment(sketch, "E18.5", {"start": v(73.55, 15.28) * mm, "end": v(74.95, -5.13) * mm});
            skLineSegment(sketch, "E18.6", {"start": v(74.95, -5.13) * mm, "end": v(70.78, -25.16) * mm});
            skLineSegment(sketch, "E18.7", {"start": v(70.78, -25.16) * mm, "end": v(61.37, -43.32) * mm});
            skLineSegment(sketch, "E18.8", {"start": v(61.37, -43.32) * mm, "end": v(47.4, -58.27) * mm});
            skLineSegment(sketch, "E18.9", {"start": v(47.4, -58.27) * mm, "end": v(29.93, -68.9) * mm});
            skLineSegment(sketch, "E18.10", {"start": v(29.93, -68.9) * mm, "end": v(10.23, -74.42) * mm});
            skLineSegment(sketch, "E18.11", {"start": v(10.23, -74.42) * mm, "end": v(-10.23, -74.42) * mm});
            skLineSegment(sketch, "E18.12", {"start": v(-10.23, -74.42) * mm, "end": v(-29.93, -68.9) * mm});
            skLineSegment(sketch, "E18.13", {"start": v(-29.93, -68.9) * mm, "end": v(-47.4, -58.27) * mm});
            skLineSegment(sketch, "E18.14", {"start": v(-47.4, -58.27) * mm, "end": v(-61.37, -43.32) * mm});
            skLineSegment(sketch, "E18.15", {"start": v(-61.37, -43.32) * mm, "end": v(-70.78, -25.16) * mm});
            skLineSegment(sketch, "E18.16", {"start": v(-70.78, -25.16) * mm, "end": v(-74.95, -5.13) * mm});
            skLineSegment(sketch, "E18.17", {"start": v(-74.95, -5.13) * mm, "end": v(-73.55, 15.28) * mm});
            skLineSegment(sketch, "E18.18", {"start": v(-73.55, 15.28) * mm, "end": v(-66.7, 34.56) * mm});
            skLineSegment(sketch, "E18.19", {"start": v(-66.7, 34.56) * mm, "end": v(-54.9, 51.27) * mm});
            skLineSegment(sketch, "E18.20", {"start": v(-54.9, 51.27) * mm, "end": v(-39.03, 64.18) * mm});
            skLineSegment(sketch, "E18.21", {"start": v(-39.03, 64.18) * mm, "end": v(-20.27, 72.33) * mm});
            skLineSegment(sketch, "E18.22", {"start": v(-20.27, 72.33) * mm, "end": v(0, 75.12) * mm});
            skSolve(sketch);
        }
        {
            var Q0;
            Q0=qCreatedBy(id+"F37.planeOp",FACE);
            cPlane(context, id + "F39", {"entities" : qUnion([Q0]), "cplaneType" : CPlaneType.OFFSET, "offset" : 100 * mm, "width" : 150 * mm, "height" : 150 * mm});
        }
        {
            var Q0;
            Q0=qCreatedBy(id+"F39.planeOp",FACE);
            var sketch = newSketch(context, id + "F40", { "sketchPlane" : qUnion([Q0])});
            skCircle(sketch, "E19.cCircle", {"center": v(0, 0) * mm, "radius": 48.81 * mm, "construction": true});
            skLineSegment(sketch, "E19.0", {"start": v(0, 48.81) * mm, "end": v(12.63, 47.15) * mm});
            skLineSegment(sketch, "E19.1", {"start": v(12.63, 47.15) * mm, "end": v(24.4, 42.27) * mm});
            skLineSegment(sketch, "E19.2", {"start": v(24.4, 42.27) * mm, "end": v(34.52, 34.52) * mm});
            skLineSegment(sketch, "E19.3", {"start": v(34.52, 34.52) * mm, "end": v(42.27, 24.4) * mm});
            skLineSegment(sketch, "E19.4", {"start": v(42.27, 24.4) * mm, "end": v(47.15, 12.63) * mm});
            skLineSegment(sketch, "E19.5", {"start": v(47.15, 12.63) * mm, "end": v(48.81, 0) * mm});
            skLineSegment(sketch, "E19.6", {"start": v(48.81, 0) * mm, "end": v(47.15, -12.63) * mm});
            skLineSegment(sketch, "E19.7", {"start": v(47.15, -12.63) * mm, "end": v(42.27, -24.4) * mm});
            skLineSegment(sketch, "E19.8", {"start": v(42.27, -24.4) * mm, "end": v(34.52, -34.52) * mm});
            skLineSegment(sketch, "E19.9", {"start": v(34.52, -34.52) * mm, "end": v(24.4, -42.27) * mm});
            skLineSegment(sketch, "E19.10", {"start": v(24.4, -42.27) * mm, "end": v(12.63, -47.15) * mm});
            skLineSegment(sketch, "E19.11", {"start": v(12.63, -47.15) * mm, "end": v(0, -48.81) * mm});
            skLineSegment(sketch, "E19.12", {"start": v(0, -48.81) * mm, "end": v(-12.63, -47.15) * mm});
            skLineSegment(sketch, "E19.13", {"start": v(-12.63, -47.15) * mm, "end": v(-24.4, -42.27) * mm});
            skLineSegment(sketch, "E19.14", {"start": v(-24.4, -42.27) * mm, "end": v(-34.52, -34.52) * mm});
            skLineSegment(sketch, "E19.15", {"start": v(-34.52, -34.52) * mm, "end": v(-42.27, -24.4) * mm});
            skLineSegment(sketch, "E19.16", {"start": v(-42.27, -24.4) * mm, "end": v(-47.15, -12.63) * mm});
            skLineSegment(sketch, "E19.17", {"start": v(-47.15, -12.63) * mm, "end": v(-48.81, 0) * mm});
            skLineSegment(sketch, "E19.18", {"start": v(-48.81, 0) * mm, "end": v(-47.15, 12.63) * mm});
            skLineSegment(sketch, "E19.19", {"start": v(-47.15, 12.63) * mm, "end": v(-42.27, 24.4) * mm});
            skLineSegment(sketch, "E19.20", {"start": v(-42.27, 24.4) * mm, "end": v(-34.52, 34.52) * mm});
            skLineSegment(sketch, "E19.21", {"start": v(-34.52, 34.52) * mm, "end": v(-24.4, 42.27) * mm});
            skLineSegment(sketch, "E19.22", {"start": v(-24.4, 42.27) * mm, "end": v(-12.63, 47.15) * mm});
            skLineSegment(sketch, "E19.23", {"start": v(-12.63, 47.15) * mm, "end": v(0, 48.81) * mm});
            skSolve(sketch);
        }
        {
            var Q0;
            Q0=qCreatedBy(id+"F39.planeOp",FACE);
            cPlane(context, id + "F41", {"entities" : qUnion([Q0]), "cplaneType" : CPlaneType.OFFSET, "offset" : 100 * mm, "width" : 150 * mm, "height" : 150 * mm});
        }
        {
            var Q0;
            Q0=qCreatedBy(id+"F41.planeOp",FACE);
            var sketch = newSketch(context, id + "F42", { "sketchPlane" : qUnion([Q0])});
            skCircle(sketch, "E20.cCircle", {"center": v(0, 0) * mm, "radius": 34.93 * mm, "construction": true});
            skLineSegment(sketch, "E20.0", {"start": v(-18.78, 29.45) * mm, "end": v(-10.87, 33.2) * mm});
            skLineSegment(sketch, "E20.1", {"start": v(-10.87, 33.2) * mm, "end": v(-2.27, 34.86) * mm});
            skLineSegment(sketch, "E20.2", {"start": v(-2.27, 34.86) * mm, "end": v(6.47, 34.33) * mm});
            skLineSegment(sketch, "E20.3", {"start": v(6.47, 34.33) * mm, "end": v(14.8, 31.64) * mm});
            skLineSegment(sketch, "E20.4", {"start": v(14.8, 31.64) * mm, "end": v(22.2, 26.97) * mm});
            skLineSegment(sketch, "E20.5", {"start": v(22.2, 26.97) * mm, "end": v(28.22, 20.6) * mm});
            skLineSegment(sketch, "E20.6", {"start": v(28.22, 20.6) * mm, "end": v(32.45, 12.93) * mm});
            skLineSegment(sketch, "E20.7", {"start": v(32.45, 12.93) * mm, "end": v(34.65, 4.45) * mm});
            skLineSegment(sketch, "E20.8", {"start": v(34.65, 4.45) * mm, "end": v(34.67, -4.3) * mm});
            skLineSegment(sketch, "E20.9", {"start": v(34.67, -4.3) * mm, "end": v(32.5, -12.79) * mm});
            skLineSegment(sketch, "E20.10", {"start": v(32.5, -12.79) * mm, "end": v(28.3, -20.47) * mm});
            skLineSegment(sketch, "E20.11", {"start": v(28.3, -20.47) * mm, "end": v(22.33, -26.87) * mm});
            skLineSegment(sketch, "E20.12", {"start": v(22.33, -26.87) * mm, "end": v(14.94, -31.58) * mm});
            skLineSegment(sketch, "E20.13", {"start": v(14.94, -31.58) * mm, "end": v(6.62, -34.3) * mm});
            skLineSegment(sketch, "E20.14", {"start": v(6.62, -34.3) * mm, "end": v(-2.12, -34.87) * mm});
            skLineSegment(sketch, "E20.15", {"start": v(-2.12, -34.87) * mm, "end": v(-10.72, -33.25) * mm});
            skLineSegment(sketch, "E20.16", {"start": v(-10.72, -33.25) * mm, "end": v(-18.65, -29.54) * mm});
            skLineSegment(sketch, "E20.17", {"start": v(-18.65, -29.54) * mm, "end": v(-25.41, -23.97) * mm});
            skLineSegment(sketch, "E20.18", {"start": v(-25.41, -23.97) * mm, "end": v(-30.58, -16.9) * mm});
            skLineSegment(sketch, "E20.19", {"start": v(-30.58, -16.9) * mm, "end": v(-33.82, -8.76) * mm});
            skLineSegment(sketch, "E20.20", {"start": v(-33.82, -8.76) * mm, "end": v(-34.93, -0.08) * mm});
            skLineSegment(sketch, "E20.21", {"start": v(-34.93, -0.08) * mm, "end": v(-33.86, 8.61) * mm});
            skLineSegment(sketch, "E20.22", {"start": v(-33.86, 8.61) * mm, "end": v(-30.65, 16.76) * mm});
            skLineSegment(sketch, "E20.23", {"start": v(-30.65, 16.76) * mm, "end": v(-25.52, 23.86) * mm});
            skLineSegment(sketch, "E20.24", {"start": v(-25.52, 23.86) * mm, "end": v(-18.78, 29.45) * mm});
            skSolve(sketch);
        }
        {
            var Q0;
            Q0=qCreatedBy(id+"F41.planeOp",FACE);
            cPlane(context, id + "F43", {"entities" : qUnion([Q0]), "cplaneType" : CPlaneType.OFFSET, "offset" : 100 * mm, "width" : 150 * mm, "height" : 150 * mm});
        }
        {
            var Q0;
            Q0=qCreatedBy(id+"F43.planeOp",FACE);
            var sketch = newSketch(context, id + "F44", { "sketchPlane" : qUnion([Q0])});
            skCircle(sketch, "E21", {"center": v(0, 0) * mm, "radius": 25.1 * mm});
            skSolve(sketch);
        }
        {
            var Q0;
            Q0 = qSketchRegion(id + "F0", true);
            var Q1;
            Q1 = qSketchRegion(id + "F2", true);
            var Q2;
            Q2 = qSketchRegion(id + "F4", true);
            var Q3;
            Q3 = qSketchRegion(id + "F6", true);
            var Q4;
            Q4 = qSketchRegion(id + "F8", true);
            var Q5;
            Q5 = qSketchRegion(id + "F10", true);
            var Q6;
            Q6 = qSketchRegion(id + "F12", true);
            var Q7;
            Q7 = qSketchRegion(id + "F15", true);
            var Q8;
            Q8 = qSketchRegion(id + "F17", true);
            var Q9;
            Q9 = qSketchRegion(id + "F20", true);
            var Q10;
            Q10 = qSketchRegion(id + "F22", true);
            var Q11;
            Q11 = qSketchRegion(id + "F24", true);
            var Q12;
            Q12 = qSketchRegion(id + "F26", true);
            var Q13;
            Q13 = qSketchRegion(id + "F28", true);
            var Q14;
            Q14 = qSketchRegion(id + "F30", true);
            var Q15;
            Q15 = qSketchRegion(id + "F32", true);
            var Q16;
            Q16 = qSketchRegion(id + "F34", true);
            var Q17;
            Q17 = qSketchRegion(id + "F36", true);
            var Q18;
            Q18 = qSketchRegion(id + "F38", true);
            var Q19;
            Q19 = qSketchRegion(id + "F40", true);
            var Q20;
            Q20 = qSketchRegion(id + "F42", true);
            var Q21;
            Q21=sQuery(id+"F44.wireOp",VERTEX,"E21.center");
            loft(context, id + "F45", {"sheetProfilesArray" : [{ "sheetProfileEntities" : qUnion([Q0]) }, { "sheetProfileEntities" : qUnion([Q1]) }, { "sheetProfileEntities" : qUnion([Q2]) }, { "sheetProfileEntities" : qUnion([Q3]) }, { "sheetProfileEntities" : qUnion([Q4]) }, { "sheetProfileEntities" : qUnion([Q5]) }, { "sheetProfileEntities" : qUnion([Q6]) }, { "sheetProfileEntities" : qUnion([Q7]) }, { "sheetProfileEntities" : qUnion([Q8]) }, { "sheetProfileEntities" : qUnion([Q9]) }, { "sheetProfileEntities" : qUnion([Q10]) }, { "sheetProfileEntities" : qUnion([Q11]) }, { "sheetProfileEntities" : qUnion([Q12]) }, { "sheetProfileEntities" : qUnion([Q13]) }, { "sheetProfileEntities" : qUnion([Q14]) }, { "sheetProfileEntities" : qUnion([Q15]) }, { "sheetProfileEntities" : qUnion([Q16]) }, { "sheetProfileEntities" : qUnion([Q17]) }, { "sheetProfileEntities" : qUnion([Q18]) }, { "sheetProfileEntities" : qUnion([Q19]) }, { "sheetProfileEntities" : qUnion([Q20]) }, { "sheetProfileEntities" : qUnion([Q21]) }]});
        }
    });
